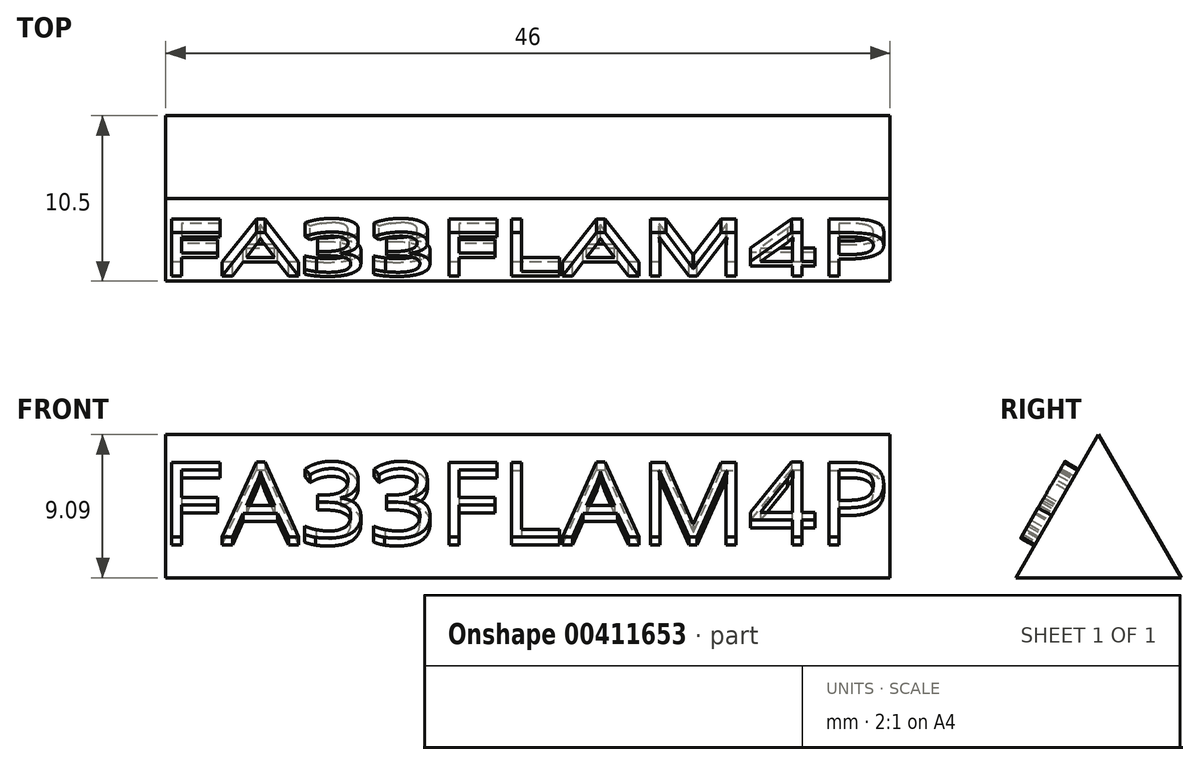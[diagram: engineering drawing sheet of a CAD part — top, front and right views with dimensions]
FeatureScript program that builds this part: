
annotation { "Feature Type Name" : "Feature", "Feature Type Description" : "" }
export const myFeature = defineFeature(function(context is Context, id is Id, definition is map)
    precondition{}
    {
        {
            var Q0;
            Q0=qCreatedBy(makeId("Right.planeOp"),FACE);
            var sketch = newSketch(context, id + "F0", { "sketchPlane" : qUnion([Q0])});
            skCircle(sketch, "E0", {"center": v(0, 0) * mm, "radius": 6.06 * mm, "construction": true});
            skLineSegment(sketch, "E1", {"start": v(0, 6.06) * mm, "end": v(0, 0) * mm, "construction": true});
            skLineSegment(sketch, "E2", {"start": v(0, 0) * mm, "end": v(-6.74, -3.9) * mm, "construction": true});
            skLineSegment(sketch, "E3", {"start": v(0, 0) * mm, "end": v(7.07, -4.08) * mm, "construction": true});
            skLineSegment(sketch, "E4", {"start": v(-5.25, -3.03) * mm, "end": v(5.25, -3.03) * mm});
            skLineSegment(sketch, "E5", {"start": v(-5.25, -3.03) * mm, "end": v(0, 6.06) * mm});
            skLineSegment(sketch, "E6", {"start": v(0, 6.06) * mm, "end": v(5.25, -3.03) * mm});
            skSolve(sketch);
        }
        {
            var Q0;
            Q0=makeQuery(id+"F0.imprint","IMPRINT",FACE,{"disambiguationData":[TD([[makeQuery(id+"F0.imprint","IMPRINT",EDGE,{"derivedFrom":sQuery(id+"F0.wireOp",EDGE,"E4")}),1.0]])]});
            extrude(context, id + "F1", {"entities" : qUnion([Q0]), "depth" : 46 * mm});
        }
        {
            var Q0;
            Q0=makeQuery(id+"F1.opExtrude","SWEPT_FACE",FACE,{"disambiguationData":[OSD([sQuery(id+"F0.wireOp",EDGE,"E5")])]});
            var sketch = newSketch(context, id + "F2", { "sketchPlane" : qUnion([Q0])});
            skText(sketch, "E7", { "text": "FA33FLAM4P", "fontName": "OpenSans-Regular.ttf"});
            const initialGuessF2  = {"E7": [-0.00037, -0.00285, 1, 0, 0.00553]};
            skSetInitialGuess(sketch, initialGuessF2);
            skSolve(sketch);
        }
        {
            var Q0;
            Q0 = qSketchRegion(id + "F2", true);
            extrude(context, id + "F3", {"entities" : qUnion([Q0]), "operationType" : NewBodyOperationType.ADD, "depth" : 1 * mm});
        }
    });
